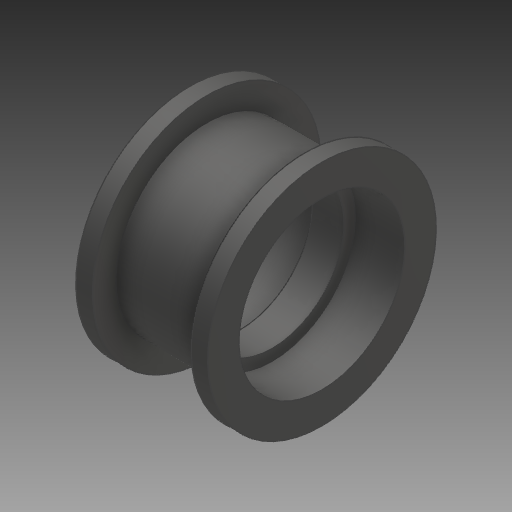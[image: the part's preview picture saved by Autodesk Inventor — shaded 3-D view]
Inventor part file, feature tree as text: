
AUTODESK INVENTOR PART (.ipt)
format: ipt  version: 2017 (Build 210142000, 142)  size: 164,352 bytes
history: mixed  units: mm
features: revolve x1, imported_body x1
ambient origin geometry x8: Origin, YZ Plane, XZ Plane, XY Plane, X Axis, Y Axis, Z Axis, Center Point
bodies: Solid1 (imported_parasolid)
feature tree (2):
  revolve  "Revolve1"  [1 undecoded]
  imported_body  NMx_Import_Brep_tag  [imported B-rep: ~12 faces, bbox_mm=[12.7, 0.0, 4.05]]
note: 1 required parameter value undecoded (feature->parameter linkage not recoverable at this tier; creation-order binding heuristic only, values carry confidence <= 0.55)
